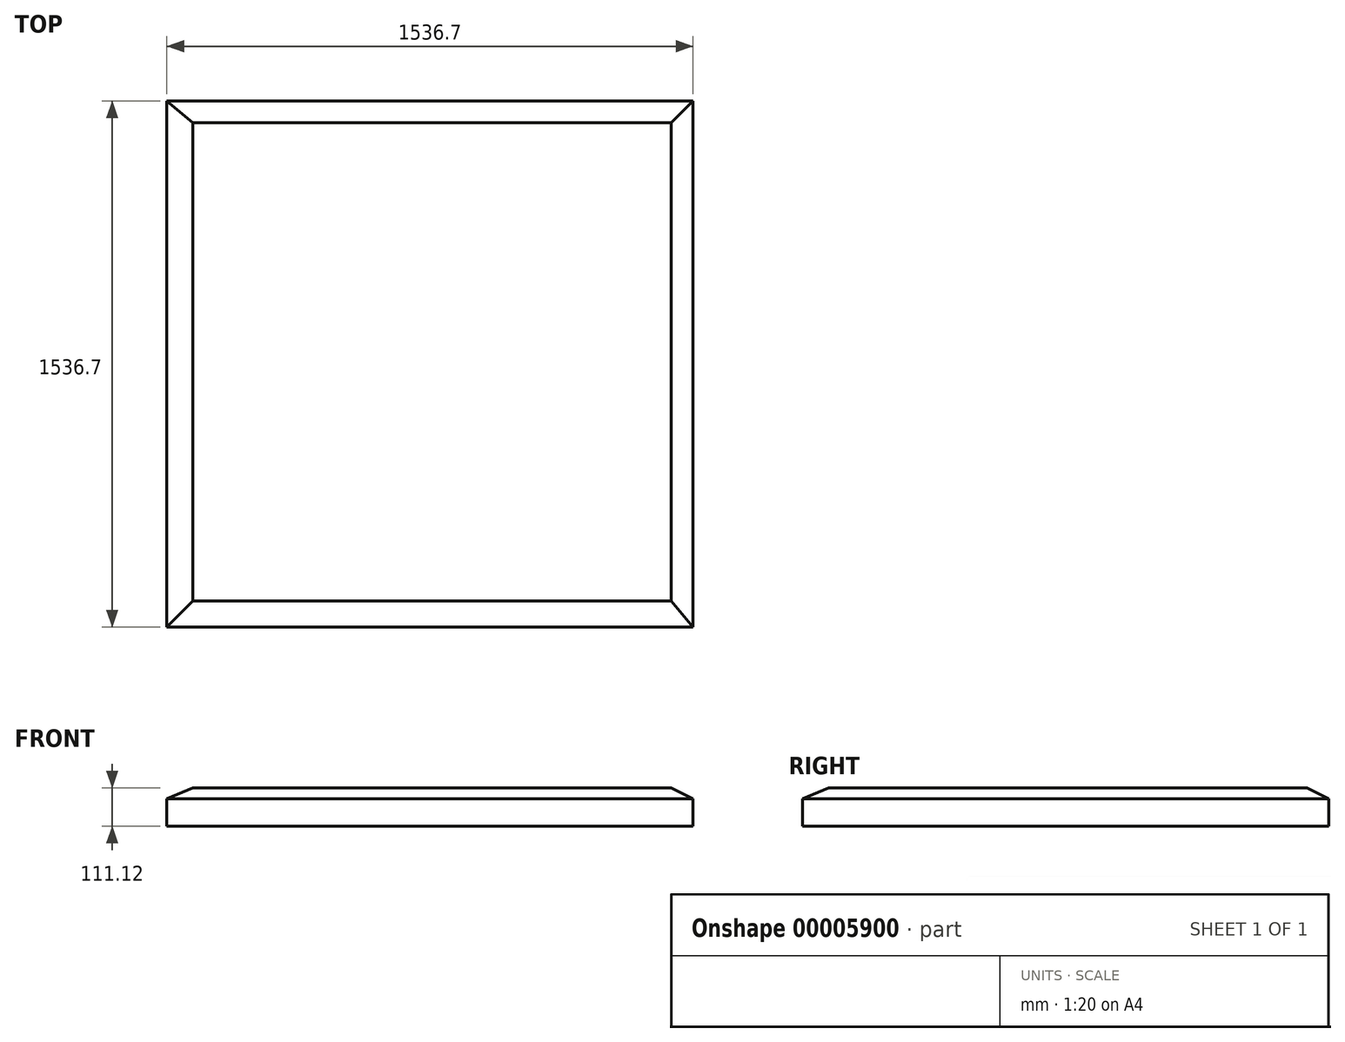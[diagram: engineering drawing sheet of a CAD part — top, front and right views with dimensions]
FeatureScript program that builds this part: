
annotation { "Feature Type Name" : "Feature", "Feature Type Description" : "" }
export const myFeature = defineFeature(function(context is Context, id is Id, definition is map)
    precondition{}
    {
        {
            var Q0;
            Q0=qCreatedBy(makeId("Top.planeOp"),FACE);
            var sketch = newSketch(context, id + "F0", { "sketchPlane" : qUnion([Q0])});
            skLineSegment(sketch, "E0.bottom", {"start": v(0, 0) * mm, "end": v(1536.7, 0) * mm});
            skLineSegment(sketch, "E0.top", {"start": v(0, 1536.7) * mm, "end": v(1536.7, 1536.7) * mm});
            skLineSegment(sketch, "E0.left", {"start": v(0, 0) * mm, "end": v(0, 1536.7) * mm});
            skLineSegment(sketch, "E0.right", {"start": v(1536.7, 0) * mm, "end": v(1536.7, 1536.7) * mm});
            skSolve(sketch);
        }
        {
            var Q0;
            Q0=makeQuery(id+"F0.imprint","IMPRINT",FACE,{"disambiguationData":[TD([[makeQuery(id+"F0.imprint","IMPRINT",EDGE,{"derivedFrom":sQuery(id+"F0.wireOp",EDGE,"E0.bottom")}),1.0]])]});
            extrude(context, id + "F1", {"entities" : qUnion([Q0]), "depth" : 79.38 * mm});
        }
        {
            var Q0;
            Q0=makeQuery(id+"F1.opExtrude","CAP_FACE",FACE,{"disambiguationData":[OSD([sQuery(id+"F0.wireOp",EDGE,"E0.bottom"),sQuery(id+"F0.wireOp",EDGE,"E0.top"),sQuery(id+"F0.wireOp",EDGE,"E0.left"),sQuery(id+"F0.wireOp",EDGE,"E0.right")])],"isStart":false});
            cPlane(context, id + "F2", {"entities" : qUnion([Q0]), "cplaneType" : CPlaneType.OFFSET, "offset" : 31.75 * mm, "width" : 152.4 * mm, "height" : 152.4 * mm});
        }
        {
            var Q0;
            Q0=qCreatedBy(id+"F2.planeOp",FACE);
            var sketch = newSketch(context, id + "F3", { "sketchPlane" : qUnion([Q0])});
            skLineSegment(sketch, "E1.bottom", {"start": v(76.2, 1473.2) * mm, "end": v(1473.2, 1473.2) * mm});
            skLineSegment(sketch, "E1.top", {"start": v(76.2, 76.2) * mm, "end": v(1473.2, 76.2) * mm});
            skLineSegment(sketch, "E1.left", {"start": v(76.2, 1473.2) * mm, "end": v(76.2, 76.2) * mm});
            skLineSegment(sketch, "E1.right", {"start": v(1473.2, 1473.2) * mm, "end": v(1473.2, 76.2) * mm});
            skLineSegment(sketch, "E2.0", {"start": v(0, 1536.7) * mm, "end": v(1536.7, 1536.7) * mm, "construction": true});
            skLineSegment(sketch, "E3.0", {"start": v(1536.7, 0) * mm, "end": v(1536.7, 1536.7) * mm, "construction": true});
            skLineSegment(sketch, "E4", {"start": v(740.66, 1536.7) * mm, "end": v(740.66, 1473.2) * mm, "construction": true});
            skLineSegment(sketch, "E5", {"start": v(1473.2, 679.35) * mm, "end": v(1536.7, 679.35) * mm, "construction": true});
            skSolve(sketch);
        }
        {
            var Q0;
            Q0=makeQuery(id+"F1.opExtrude","CAP_FACE",FACE,{"disambiguationData":[OSD([sQuery(id+"F0.wireOp",EDGE,"E0.bottom"),sQuery(id+"F0.wireOp",EDGE,"E0.top"),sQuery(id+"F0.wireOp",EDGE,"E0.left"),sQuery(id+"F0.wireOp",EDGE,"E0.right")])],"isStart":false});
            var sketch = newSketch(context, id + "F4", { "sketchPlane" : qUnion([Q0])});
            skLineSegment(sketch, "E6.bottom", {"start": v(0, 1536.7) * mm, "end": v(1536.7, 1536.7) * mm});
            skLineSegment(sketch, "E6.top", {"start": v(0, 0) * mm, "end": v(1536.7, 0) * mm});
            skLineSegment(sketch, "E6.left", {"start": v(0, 1536.7) * mm, "end": v(0, 0) * mm});
            skLineSegment(sketch, "E6.right", {"start": v(1536.7, 1536.7) * mm, "end": v(1536.7, 0) * mm});
            skSolve(sketch);
        }
        {
            var Q0;
            Q0=makeQuery(id+"F3.imprint","IMPRINT",FACE,{"disambiguationData":[TD([[makeQuery(id+"F3.imprint","IMPRINT",EDGE,{"derivedFrom":sQuery(id+"F3.wireOp",EDGE,"E1.bottom")}),-1.0]])]});
            var Q1;
            Q1=makeQuery(id+"F4.imprint","IMPRINT",FACE,{"disambiguationData":[TD([[makeQuery(id+"F4.imprint","IMPRINT",EDGE,{"derivedFrom":sQuery(id+"F4.wireOp",EDGE,"E6.bottom")}),-1.0]])]});
            loft(context, id + "F5", {"sheetProfilesArray" : [{ "sheetProfileEntities" : qUnion([Q0]) }, { "sheetProfileEntities" : qUnion([Q1]) }]});
        }
    });
